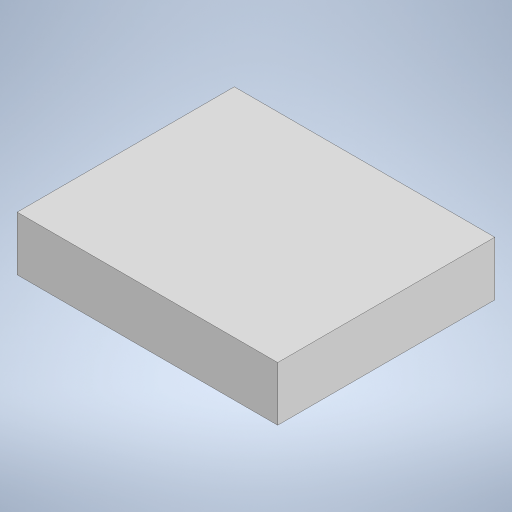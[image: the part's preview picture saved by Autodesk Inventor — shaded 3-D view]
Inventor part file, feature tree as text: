
AUTODESK INVENTOR PART (.ipt)
format: ipt  version: 2024.2 (Build 282272000, 272)  size: 187,904 bytes
history: native  units: in
note: dims shown in document units (in); Inventor stores cm internally (conversion verified against a paired STEP export)
features: extrude x1, sketch x1
ambient origin geometry x8: Origin, YZ Plane, XZ Plane, XY Plane, X Axis, Y Axis, Z Axis, Center Point
bodies: Solid1 (feature_tree)
feature tree (2):
  extrude  "Extrusion1"  Depth=0.25in
  sketch  "Sketch1"  dims[d5=0.3in d6=0.25in d7=0.0625in d8=0.0in]
